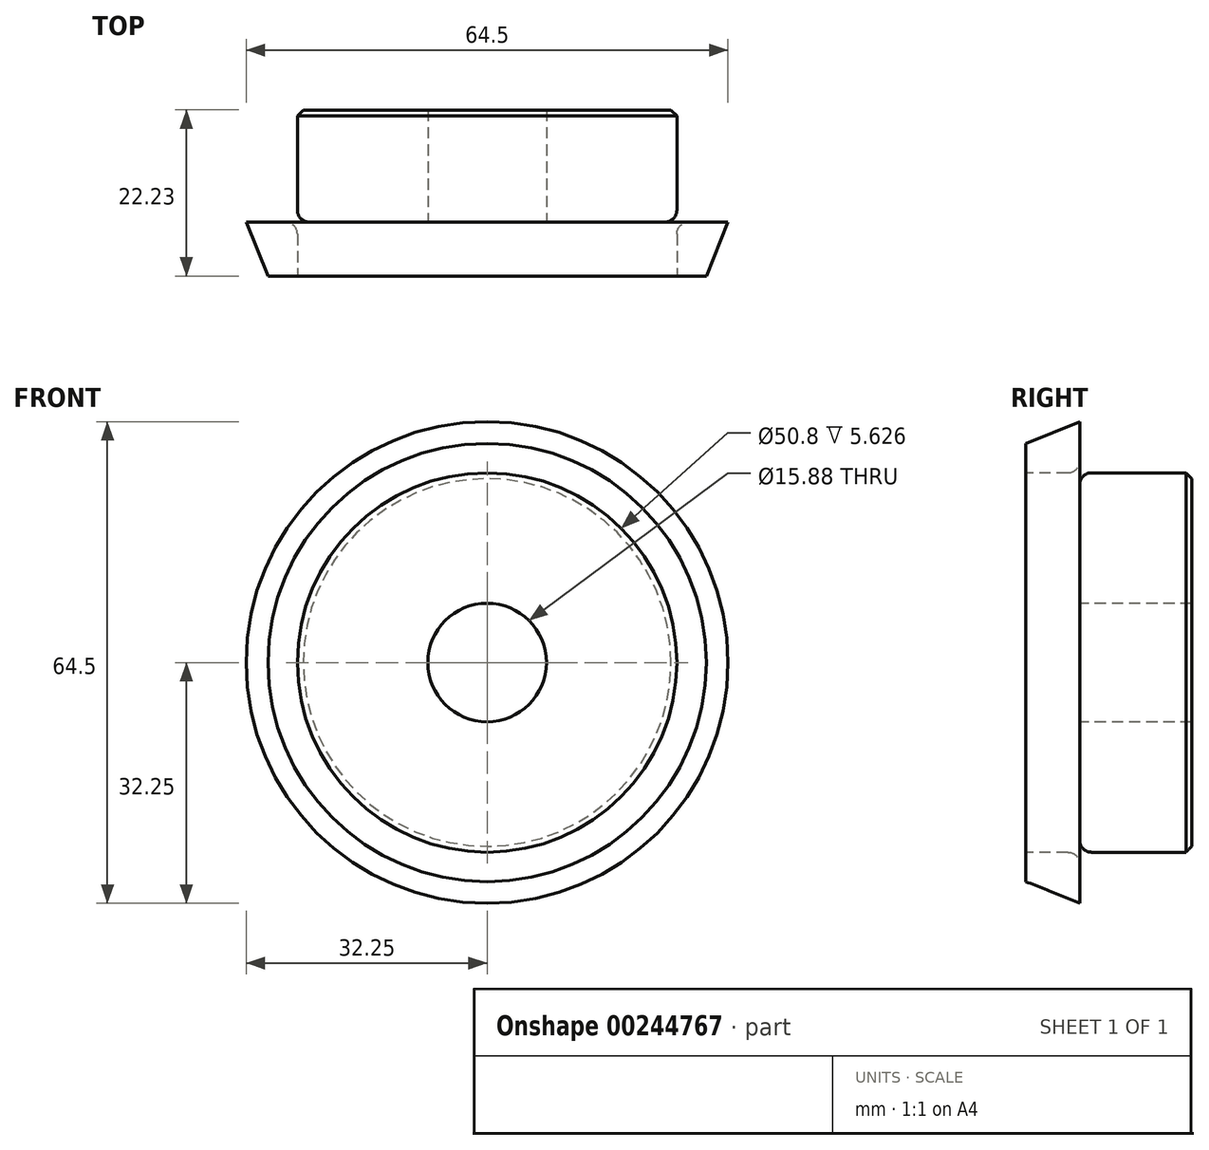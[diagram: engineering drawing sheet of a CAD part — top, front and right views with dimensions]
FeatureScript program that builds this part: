
annotation { "Feature Type Name" : "Feature", "Feature Type Description" : "" }
export const myFeature = defineFeature(function(context is Context, id is Id, definition is map)
    precondition{}
    {
        {
            var Q0;
            Q0=qCreatedBy(makeId("Right.planeOp"),FACE);
            var sketch = newSketch(context, id + "F0", { "sketchPlane" : qUnion([Q0])});
            skLineSegment(sketch, "E0", {"start": v(0, 0) * mm, "end": v(22.22, 0) * mm, "construction": true});
            skLineSegment(sketch, "E1.bottom", {"start": v(0, 7.94) * mm, "end": v(7.21, 7.94) * mm});
            skLineSegment(sketch, "E1.top", {"start": v(0, 35.69) * mm, "end": v(7.21, 35.69) * mm});
            skLineSegment(sketch, "E1.left", {"start": v(0, 7.94) * mm, "end": v(0, 35.69) * mm});
            skLineSegment(sketch, "E1.right", {"start": v(7.21, 7.94) * mm, "end": v(7.21, 35.69) * mm});
            skLineSegment(sketch, "E2.bottom", {"start": v(0, 7.94) * mm, "end": v(22.22, 7.94) * mm});
            skLineSegment(sketch, "E2.top", {"start": v(0, 25.4) * mm, "end": v(22.23, 25.4) * mm});
            skLineSegment(sketch, "E2.left", {"start": v(0, 7.94) * mm, "end": v(0, 25.4) * mm});
            skLineSegment(sketch, "E2.right", {"start": v(22.22, 7.94) * mm, "end": v(22.22, 25.4) * mm});
            skLineSegment(sketch, "E3.MirrorCS", {"start": v(0, -7.94) * mm, "end": v(7.21, -7.94) * mm});
            skLineSegment(sketch, "E4.MirrorCS", {"start": v(0, -7.94) * mm, "end": v(0, -25.4) * mm});
            skLineSegment(sketch, "E5.MirrorCS", {"start": v(0, -7.94) * mm, "end": v(22.23, -7.94) * mm});
            skLineSegment(sketch, "E6.MirrorCS", {"start": v(0, -25.4) * mm, "end": v(22.23, -25.4) * mm});
            skLineSegment(sketch, "E7.MirrorCS", {"start": v(22.23, -7.94) * mm, "end": v(22.23, -25.4) * mm});
            skLineSegment(sketch, "E8.MirrorCS", {"start": v(7.21, -7.94) * mm, "end": v(7.21, -35.69) * mm});
            skLineSegment(sketch, "E9.MirrorCS", {"start": v(0, -7.94) * mm, "end": v(0, -35.69) * mm});
            skLineSegment(sketch, "E10.MirrorCS", {"start": v(0, -35.69) * mm, "end": v(7.21, -35.69) * mm});
            skSolve(sketch);
        }
        {
            var Q0;
            {var subQ5=sQuery(id+"F0.wireOp",EDGE,"E2.right");Q0=makeQuery(id+"F0.imprint","IMPRINT",FACE,{"disambiguationData":[TD([[makeQuery(id+"F0.imprint","IMPRINT",EDGE,{"derivedFrom":subQ5}),1.0]])]});}
            var Q1;
            {var subQ5=sQuery(id+"F0.wireOp",EDGE,"E2.left");Q1=makeQuery(id+"F0.imprint","IMPRINT",FACE,{"disambiguationData":[TD([[makeQuery(id+"F0.imprint","IMPRINT",EDGE,{"derivedFrom":subQ5}),-1.0]])]});}
            var Q2;
            {var subQ0=sQuery(id+"F0.wireOp",EDGE,"E1.top");Q2=makeQuery(id+"F0.imprint","IMPRINT",FACE,{"disambiguationData":[TD([[makeQuery(id+"F0.imprint","IMPRINT",EDGE,{"derivedFrom":subQ0}),-1.0]])]});}
            var Q3;
            Q3=sQuery(id+"F0.wireOp",EDGE,"E0");
            revolve(context, id + "F1", {"entities" : qUnion([Q0, Q1, Q2]), "axis" : qUnion([Q3]), "revolveType" : RevolveType.FULL});
        }
        {
            var Q0;
            Q0=makeQuery(id+"F1.opRevolve","SWEPT_EDGE",EDGE,{"disambiguationData":[OSD([sQuery(id+"F0.wireOp",EDGE,"E1.right"),sQuery(id+"F0.wireOp",EDGE,"E2.top")])]});
            fillet(context, id + "F2", {"entities" : qUnion([Q0]), "radius" : 1.59 * mm, "tangentPropagation" : true, "allowEdgeOverflow" : false});
        }
        {
            var Q0;
            Q0=makeQuery(id+"F1.opRevolve","SWEPT_EDGE",EDGE,{"disambiguationData":[OSD([sQuery(id+"F0.wireOp",EDGE,"E2.top"),sQuery(id+"F0.wireOp",EDGE,"E2.right")])]});
            chamfer(context, id + "F3", {"entities" : qUnion([Q0]), "width" : 0.8 * mm, "tangentPropagation" : true});
        }
        {
            var Q0;
            Q0=makeQuery(id+"F1.opRevolve","SWEPT_EDGE",EDGE,{"disambiguationData":[OSD([sQuery(id+"F0.wireOp",EDGE,"E1.top"),sQuery(id+"F0.wireOp",EDGE,"E1.left")])]});
            var Q1;
            {var subQ0=sQuery(id+"F0.wireOp",EDGE,"E1.right");Q1=makeQuery(id+"F2.opFillet","BLEND_EDGE",EDGE,{"blendedFrom":[makeQuery(id+"F1.opRevolve","SWEPT_EDGE",EDGE,{"disambiguationData":[OSD([subQ0,sQuery(id+"F0.wireOp",EDGE,"E2.top")])]}),makeQuery(id+"F1.opRevolve","SWEPT_FACE",FACE,{"disambiguationData":[OSD([subQ0])]})],"blendedInto":[makeQuery(id+"F1.opRevolve","SWEPT_FACE",FACE,{"disambiguationData":[OSD([subQ0])]})]});}
            chamfer(context, id + "F4", {"entities" : qUnion([Q0, Q1]), "chamferType" : ChamferType.TWO_OFFSETS, "width1" : 6.35 * mm, "oppositeDirection" : false, "width2" : 15.75 * mm, "tangentPropagation" : true});
        }
    });
